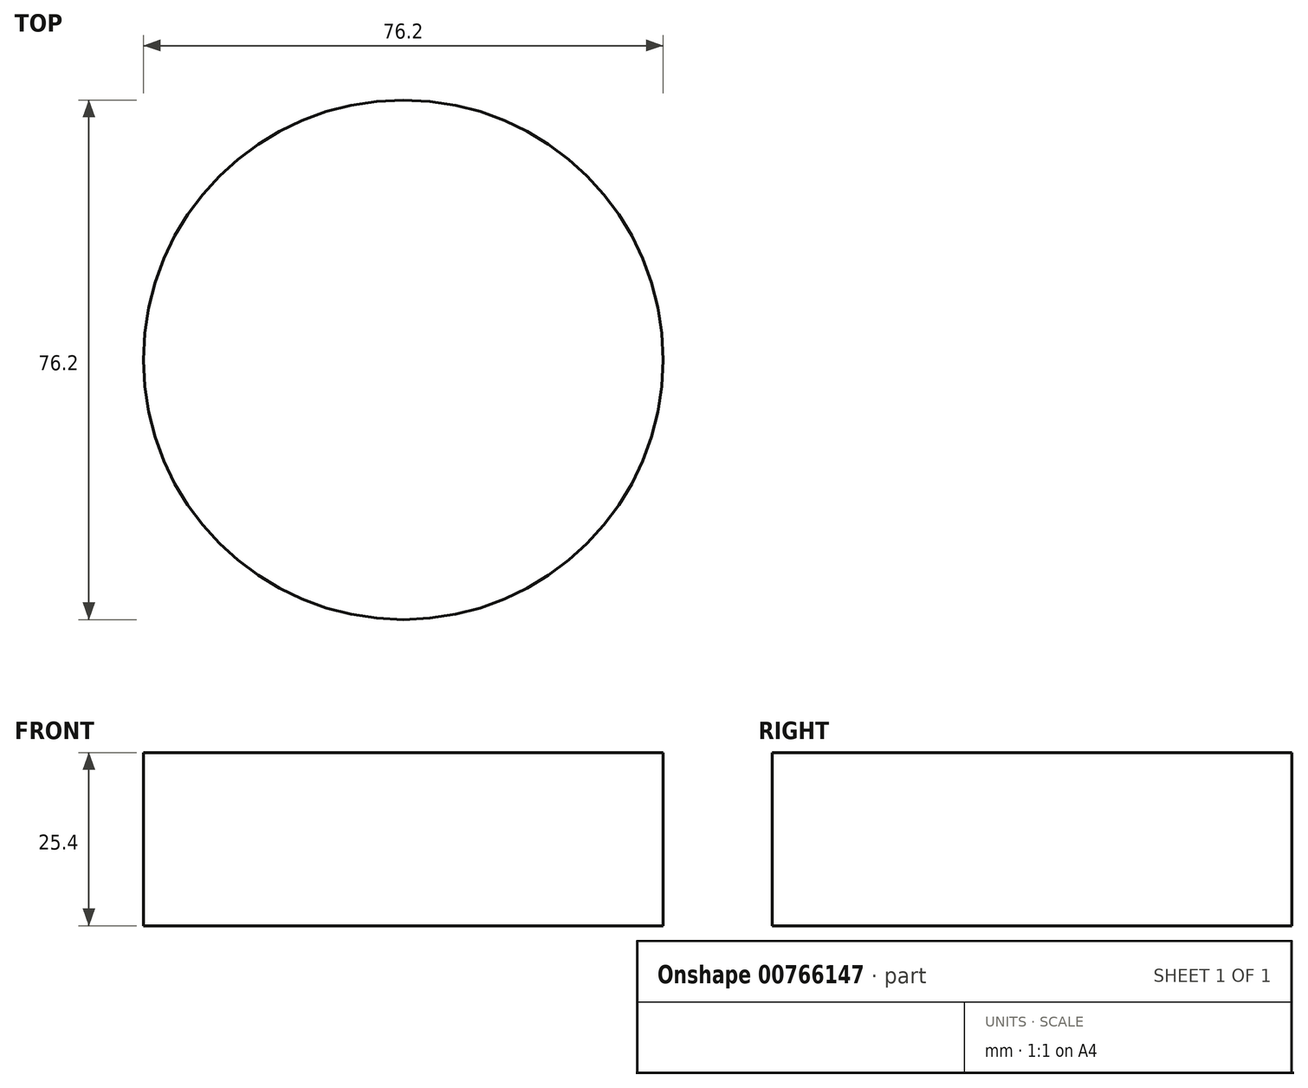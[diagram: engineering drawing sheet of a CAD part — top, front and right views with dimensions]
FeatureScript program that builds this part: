
annotation { "Feature Type Name" : "Feature", "Feature Type Description" : "" }
export const myFeature = defineFeature(function(context is Context, id is Id, definition is map)
    precondition{}
    {
        {
            var Q0;
            Q0=qCreatedBy(makeId("Top.planeOp"),FACE);
            var sketch = newSketch(context, id + "F0", { "sketchPlane" : qUnion([Q0])});
            skCircle(sketch, "E0", {"center": v(0, 0) * mm, "radius": 38.1 * mm});
            skCircle(sketch, "E1", {"center": v(0, 0) * mm, "radius": 25.4 * mm});
            skSolve(sketch);
        }
        {
            var Q0;
            Q0=makeQuery(id+"F0.imprint","IMPRINT",FACE,{"disambiguationData":[TD([[makeQuery(id+"F0.imprint","IMPRINT",EDGE,{"derivedFrom":sQuery(id+"F0.wireOp",EDGE,"E1")}),1.0]])]});
            var Q1;
            Q1=makeQuery(id+"F0.imprint","IMPRINT",FACE,{"disambiguationData":[TD([[makeQuery(id+"F0.imprint","IMPRINT",EDGE,{"derivedFrom":sQuery(id+"F0.wireOp",EDGE,"E0")}),1.0]])]});
            extrude(context, id + "F1", {"entities" : qUnion([Q0, Q1]), "depth" : -25.4 * mm, "offsetDistance" : 25.4 * mm});
        }
    });
